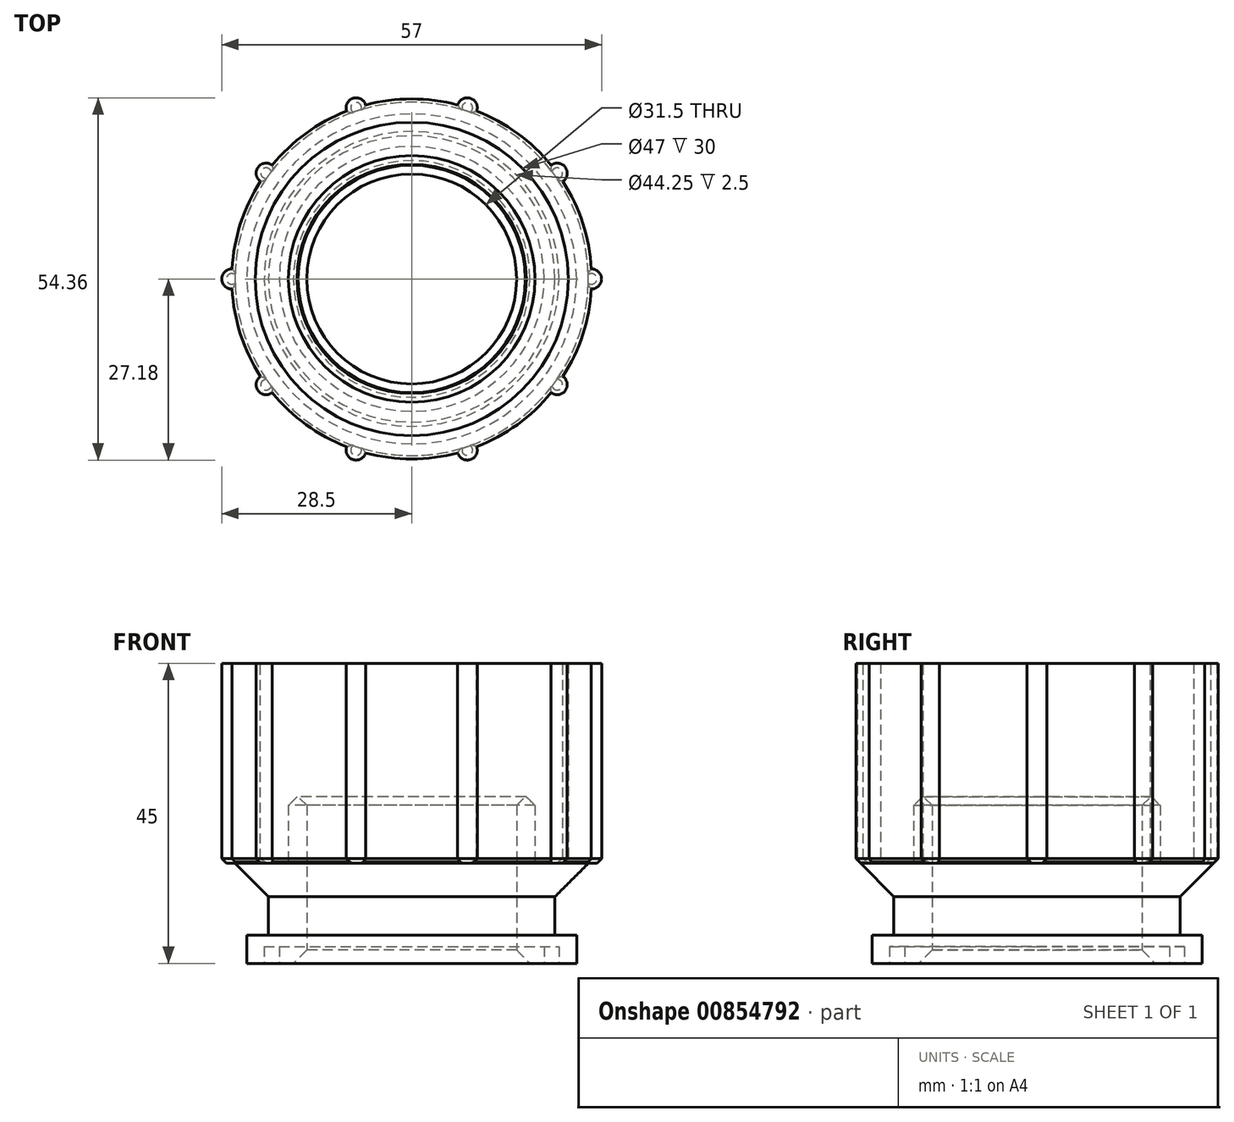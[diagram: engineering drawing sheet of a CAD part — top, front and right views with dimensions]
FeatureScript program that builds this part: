
annotation { "Feature Type Name" : "Feature", "Feature Type Description" : "" }
export const myFeature = defineFeature(function(context is Context, id is Id, definition is map)
    precondition{}
    {
        {
            var Q0;
            Q0=qCreatedBy(makeId("Top.planeOp"),FACE);
            var sketch = newSketch(context, id + "F0", { "sketchPlane" : qUnion([Q0])});
            skCircle(sketch, "E0", {"center": v(0, 0) * mm, "radius": 24.75 * mm});
            skCircle(sketch, "E1", {"center": v(0, 0) * mm, "radius": 15.75 * mm});
            skSolve(sketch);
        }
        {
            var Q0;
            Q0=makeQuery(id+"F0.imprint","IMPRINT",FACE,{"disambiguationData":[TD([[makeQuery(id+"F0.imprint","IMPRINT",EDGE,{"derivedFrom":sQuery(id+"F0.wireOp",EDGE,"E0")}),1.0]])]});
            extrude(context, id + "F1", {"entities" : qUnion([Q0]), "depth" : 4.25 * mm, "offsetDistance" : 25 * mm});
        }
        {
            var Q0;
            Q0=makeQuery(id+"F1.opExtrude","CAP_FACE",FACE,{"disambiguationData":[OSD([sQuery(id+"F0.wireOp",EDGE,"E0"),sQuery(id+"F0.wireOp",EDGE,"E1")])],"isStart":false});
            var sketch = newSketch(context, id + "F2", { "sketchPlane" : qUnion([Q0])});
            skCircle(sketch, "E2", {"center": v(0, 0) * mm, "radius": 21.5 * mm});
            skSolve(sketch);
        }
        {
            var Q0;
            Q0=makeQuery(id+"F2.imprint","IMPRINT",FACE,{"disambiguationData":[TD([[makeQuery(id+"F2.imprint","IMPRINT",EDGE,{"derivedFrom":sQuery(id+"F2.wireOp",EDGE,"E2")}),1.0]])]});
            extrude(context, id + "F3", {"entities" : qUnion([Q0]), "operationType" : NewBodyOperationType.ADD, "depth" : 4 * mm, "offsetDistance" : 25 * mm});
        }
        {
            var Q0;
            Q0=makeQuery(id+"F3.opExtrude","CAP_FACE",FACE,{"disambiguationData":[OSD([sQuery(id+"F0.wireOp",EDGE,"E1"),sQuery(id+"F2.wireOp",EDGE,"E2")])],"isStart":false});
            var sketch = newSketch(context, id + "F4", { "sketchPlane" : qUnion([Q0])});
            skCircle(sketch, "E3", {"center": v(0, 0) * mm, "radius": 26.5 * mm});
            skSolve(sketch);
        }
        {
            var Q0;
            Q0=makeQuery(id+"F4.imprint","IMPRINT",FACE,{"disambiguationData":[TD([[makeQuery(id+"F4.imprint","IMPRINT",EDGE,{"derivedFrom":sQuery(id+"F4.wireOp",EDGE,"E3")}),1.0]])]});
            var Q1;
            Q1=makeQuery(id+"F4.imprint","IMPRINT",FACE,{"disambiguationData":[TD([[makeQuery(id+"F4.imprint","IMPRINT",EDGE,{"derivedFrom":makeQuery(id+"F3.opExtrude","CAP_EDGE",EDGE,{"disambiguationData":[OSD([sQuery(id+"F2.wireOp",EDGE,"E2")])],"isStart":false})}),1.0]])]});
            extrude(context, id + "F5", {"entities" : qUnion([Q0, Q1]), "operationType" : NewBodyOperationType.ADD, "depth" : 6.75 * mm, "offsetDistance" : 25 * mm});
        }
        {
            var Q0;
            Q0=makeQuery(id+"F5.opExtrude","CAP_FACE",FACE,{"disambiguationData":[OSD([sQuery(id+"F0.wireOp",EDGE,"E1"),sQuery(id+"F4.wireOp",EDGE,"E3")])],"isStart":false});
            var sketch = newSketch(context, id + "F6", { "sketchPlane" : qUnion([Q0])});
            skCircle(sketch, "E4", {"center": v(0, 0) * mm, "radius": 27 * mm});
            skCircle(sketch, "E5", {"center": v(0, 0) * mm, "radius": 23.5 * mm});
            skSolve(sketch);
        }
        {
            var Q0;
            Q0=makeQuery(id+"F6.imprint","IMPRINT",FACE,{"disambiguationData":[TD([[makeQuery(id+"F6.imprint","IMPRINT",EDGE,{"derivedFrom":makeQuery(id+"F5.opExtrude","CAP_EDGE",EDGE,{"disambiguationData":[OSD([sQuery(id+"F4.wireOp",EDGE,"E3")])],"isStart":false})}),1.0]])]});
            var Q1;
            Q1=makeQuery(id+"F6.imprint","IMPRINT",FACE,{"disambiguationData":[TD([[makeQuery(id+"F6.imprint","IMPRINT",EDGE,{"derivedFrom":sQuery(id+"F6.wireOp",EDGE,"E4")}),1.0]])]});
            extrude(context, id + "F7", {"entities" : qUnion([Q0, Q1]), "operationType" : NewBodyOperationType.ADD, "depth" : 30 * mm, "offsetDistance" : 25 * mm});
        }
        {
            var Q0;
            Q0=makeQuery(id+"F5.opExtrude","CAP_FACE",FACE,{"disambiguationData":[OSD([sQuery(id+"F0.wireOp",EDGE,"E1"),sQuery(id+"F4.wireOp",EDGE,"E3")])],"isStart":false});
            var sketch = newSketch(context, id + "F8", { "sketchPlane" : qUnion([Q0])});
            skCircle(sketch, "E6", {"center": v(0, 0) * mm, "radius": 18.5 * mm});
            skSolve(sketch);
        }
        {
            var Q0;
            Q0=makeQuery(id+"F8.imprint","IMPRINT",FACE,{"disambiguationData":[TD([[makeQuery(id+"F8.imprint","IMPRINT",EDGE,{"derivedFrom":sQuery(id+"F8.wireOp",EDGE,"E6")}),1.0]])]});
            extrude(context, id + "F9", {"entities" : qUnion([Q0]), "operationType" : NewBodyOperationType.ADD, "depth" : 10 * mm, "offsetDistance" : 25 * mm});
        }
        {
            var Q0;
            Q0=makeQuery(id+"F1.opExtrude","CAP_FACE",FACE,{"disambiguationData":[OSD([sQuery(id+"F0.wireOp",EDGE,"E0"),sQuery(id+"F0.wireOp",EDGE,"E1")])],"isStart":true});
            var sketch = newSketch(context, id + "F10", { "sketchPlane" : qUnion([Q0])});
            skCircle(sketch, "E7", {"center": v(0, 0) * mm, "radius": 22.12 * mm});
            skCircle(sketch, "E8", {"center": v(0, 0) * mm, "radius": 19.88 * mm});
            skSolve(sketch);
        }
        {
            var Q0;
            Q0=makeQuery(id+"F10.imprint","IMPRINT",FACE,{"disambiguationData":[TD([[makeQuery(id+"F10.imprint","IMPRINT",EDGE,{"derivedFrom":sQuery(id+"F10.wireOp",EDGE,"E7")}),1.0]])]});
            extrude(context, id + "F11", {"entities" : qUnion([Q0]), "operationType" : NewBodyOperationType.REMOVE, "oppositeDirection" : true, "depth" : 2.5 * mm, "offsetDistance" : 25 * mm});
        }
        {
            var Q0;
            Q0=makeQuery(id+"F7.opExtrude","CAP_FACE",FACE,{"disambiguationData":[OSD([sQuery(id+"F6.wireOp",EDGE,"E4"),sQuery(id+"F6.wireOp",EDGE,"E5")])],"isStart":false});
            var sketch = newSketch(context, id + "F12", { "sketchPlane" : qUnion([Q0])});
            skArc(sketch, "E9", {"start": v(26.96, -1.5) * mm, "mid": v(28.5, 0) * mm, "end": v(26.96, 1.5) * mm});
            skArc(sketch, "E10.1.0", {"start": v(22.7, 14.63) * mm, "mid": v(23.06, 16.75) * mm, "end": v(20.93, 17.06) * mm});
            skArc(sketch, "E10.2.0", {"start": v(9.76, 25.18) * mm, "mid": v(8.8, 27.1) * mm, "end": v(6.9, 26.1) * mm});
            skArc(sketch, "E10.3.0", {"start": v(-6.9, 26.1) * mm, "mid": v(-8.8, 27.1) * mm, "end": v(-9.76, 25.18) * mm});
            skArc(sketch, "E10.4.0", {"start": v(-20.93, 17.06) * mm, "mid": v(-23.06, 16.75) * mm, "end": v(-22.7, 14.63) * mm});
            skArc(sketch, "E10.5.0", {"start": v(-26.96, 1.5) * mm, "mid": v(-28.5, 0) * mm, "end": v(-26.96, -1.5) * mm});
            skArc(sketch, "E10.6.0", {"start": v(-22.7, -14.63) * mm, "mid": v(-23.06, -16.75) * mm, "end": v(-20.93, -17.06) * mm});
            skArc(sketch, "E10.7.0", {"start": v(-9.76, -25.18) * mm, "mid": v(-8.8, -27.1) * mm, "end": v(-6.9, -26.1) * mm});
            skArc(sketch, "E10.8.0", {"start": v(6.9, -26.1) * mm, "mid": v(8.8, -27.1) * mm, "end": v(9.76, -25.18) * mm});
            skArc(sketch, "E10.9.0", {"start": v(20.93, -17.06) * mm, "mid": v(23.06, -16.75) * mm, "end": v(22.7, -14.63) * mm});
            skPoint(sketch, "E10.center", {"position": v(0, 0) * mm});
            skSolve(sketch);
        }
        {
            var Q0;
            {var subQ0=sQuery(id+"F12.wireOp",EDGE,"E10.1.0");Q0=makeQuery(id+"F12.imprint","IMPRINT",FACE,{"disambiguationData":[TD([[makeQuery(id+"F12.imprint","IMPRINT",EDGE,{"derivedFrom":subQ0}),1.0]])]});}
            var Q1;
            {var subQ0=sQuery(id+"F12.wireOp",EDGE,"E10.2.0");Q1=makeQuery(id+"F12.imprint","IMPRINT",FACE,{"disambiguationData":[TD([[makeQuery(id+"F12.imprint","IMPRINT",EDGE,{"derivedFrom":subQ0}),1.0]])]});}
            var Q2;
            {var subQ0=sQuery(id+"F12.wireOp",EDGE,"E10.3.0");Q2=makeQuery(id+"F12.imprint","IMPRINT",FACE,{"disambiguationData":[TD([[makeQuery(id+"F12.imprint","IMPRINT",EDGE,{"derivedFrom":subQ0}),1.0]])]});}
            var Q3;
            {var subQ0=sQuery(id+"F12.wireOp",EDGE,"E10.4.0");Q3=makeQuery(id+"F12.imprint","IMPRINT",FACE,{"disambiguationData":[TD([[makeQuery(id+"F12.imprint","IMPRINT",EDGE,{"derivedFrom":subQ0}),1.0]])]});}
            var Q4;
            {var subQ0=sQuery(id+"F12.wireOp",EDGE,"E10.5.0");Q4=makeQuery(id+"F12.imprint","IMPRINT",FACE,{"disambiguationData":[TD([[makeQuery(id+"F12.imprint","IMPRINT",EDGE,{"derivedFrom":subQ0}),1.0]])]});}
            var Q5;
            {var subQ0=sQuery(id+"F12.wireOp",EDGE,"E10.6.0");Q5=makeQuery(id+"F12.imprint","IMPRINT",FACE,{"disambiguationData":[TD([[makeQuery(id+"F12.imprint","IMPRINT",EDGE,{"derivedFrom":subQ0}),1.0]])]});}
            var Q6;
            {var subQ0=sQuery(id+"F12.wireOp",EDGE,"E10.7.0");Q6=makeQuery(id+"F12.imprint","IMPRINT",FACE,{"disambiguationData":[TD([[makeQuery(id+"F12.imprint","IMPRINT",EDGE,{"derivedFrom":subQ0}),1.0]])]});}
            var Q7;
            {var subQ0=sQuery(id+"F12.wireOp",EDGE,"E10.8.0");Q7=makeQuery(id+"F12.imprint","IMPRINT",FACE,{"disambiguationData":[TD([[makeQuery(id+"F12.imprint","IMPRINT",EDGE,{"derivedFrom":subQ0}),1.0]])]});}
            var Q8;
            {var subQ0=sQuery(id+"F12.wireOp",EDGE,"E10.9.0");Q8=makeQuery(id+"F12.imprint","IMPRINT",FACE,{"disambiguationData":[TD([[makeQuery(id+"F12.imprint","IMPRINT",EDGE,{"derivedFrom":subQ0}),1.0]])]});}
            var Q9;
            {var subQ0=sQuery(id+"F12.wireOp",EDGE,"E9");Q9=makeQuery(id+"F12.imprint","IMPRINT",FACE,{"disambiguationData":[TD([[makeQuery(id+"F12.imprint","IMPRINT",EDGE,{"derivedFrom":subQ0}),1.0]])]});}
            var Q10;
            Q10=makeQuery(id+"F7.opExtrude","CAP_FACE",FACE,{"disambiguationData":[OSD([sQuery(id+"F6.wireOp",EDGE,"E4"),sQuery(id+"F6.wireOp",EDGE,"E5")])],"isStart":true});
            extrude(context, id + "F13", {"entities" : qUnion([Q0, Q1, Q2, Q3, Q4, Q5, Q6, Q7, Q8, Q9]), "operationType" : NewBodyOperationType.ADD, "endBound" : BoundingType.UP_TO_SURFACE, "oppositeDirection" : true, "depth" : 25 * mm, "endBoundEntityFace" : qUnion([Q10]), "offsetDistance" : 25 * mm});
        }
        {
            var Q0;
            Q0=makeQuery(id+"F1.opExtrude","CAP_EDGE",EDGE,{"disambiguationData":[OSD([sQuery(id+"F0.wireOp",EDGE,"E1")])],"isStart":true});
            chamfer(context, id + "F14", {"entities" : qUnion([Q0]), "width" : 2 * mm, "tangentPropagation" : true});
        }
        {
            var Q0;
            {var subQ0=sQuery(id+"F12.wireOp",EDGE,"E10.5.0");var subQ1=sQuery(id+"F6.wireOp",EDGE,"E4");var subQ2=sQuery(id+"F12.wireOp",EDGE,"E10.6.0");Q0=makeQuery(id+"F13.boolean.opBoolean","SPLIT",EDGE,{"disambiguationData":[TD([makeQuery(id+"F7.opExtrude","SWEPT_FACE",FACE,{"disambiguationData":[OSD([subQ1])]}),makeQuery(id+"F7.opExtrude","CAP_FACE",FACE,{"disambiguationData":[OSD([subQ1,sQuery(id+"F6.wireOp",EDGE,"E5")])],"isStart":true}),makeQuery(id+"F13.opExtrude","CAP_FACE",FACE,{"disambiguationData":[OSD([subQ1,sQuery(id+"F12.wireOp",EDGE,"E9")])],"isStart":false}),makeQuery(id+"F13.opExtrude","CAP_FACE",FACE,{"disambiguationData":[OSD([subQ1,sQuery(id+"F12.wireOp",EDGE,"E10.1.0")])],"isStart":false}),makeQuery(id+"F13.opExtrude","CAP_FACE",FACE,{"disambiguationData":[OSD([subQ1,sQuery(id+"F12.wireOp",EDGE,"E10.2.0")])],"isStart":false}),makeQuery(id+"F13.opExtrude","CAP_FACE",FACE,{"disambiguationData":[OSD([subQ1,sQuery(id+"F12.wireOp",EDGE,"E10.3.0")])],"isStart":false}),makeQuery(id+"F13.opExtrude","CAP_FACE",FACE,{"disambiguationData":[OSD([subQ1,sQuery(id+"F12.wireOp",EDGE,"E10.4.0")])],"isStart":false}),makeQuery(id+"F13.opExtrude","SWEPT_FACE",FACE,{"disambiguationData":[OSD([subQ0])]}),makeQuery(id+"F13.opExtrude","CAP_FACE",FACE,{"disambiguationData":[OSD([subQ1,subQ0])],"isStart":false}),makeQuery(id+"F13.opExtrude","SWEPT_FACE",FACE,{"disambiguationData":[OSD([subQ2])]}),makeQuery(id+"F13.opExtrude","CAP_FACE",FACE,{"disambiguationData":[OSD([subQ1,subQ2])],"isStart":false}),makeQuery(id+"F13.opExtrude","CAP_FACE",FACE,{"disambiguationData":[OSD([subQ1,sQuery(id+"F12.wireOp",EDGE,"E10.7.0")])],"isStart":false}),makeQuery(id+"F13.opExtrude","CAP_FACE",FACE,{"disambiguationData":[OSD([subQ1,sQuery(id+"F12.wireOp",EDGE,"E10.8.0")])],"isStart":false}),makeQuery(id+"F13.opExtrude","CAP_FACE",FACE,{"disambiguationData":[OSD([subQ1,sQuery(id+"F12.wireOp",EDGE,"E10.9.0")])],"isStart":false})])],"derivedFrom":makeQuery(id+"F7.opExtrude","CAP_EDGE",EDGE,{"disambiguationData":[OSD([subQ1])],"isStart":true})});}
            var Q1;
            Q1=makeQuery(id+"F13.opExtrude","CAP_EDGE",EDGE,{"disambiguationData":[OSD([sQuery(id+"F12.wireOp",EDGE,"E10.5.0")])],"isStart":false});
            var Q2;
            {var subQ0=sQuery(id+"F12.wireOp",EDGE,"E10.5.0");var subQ1=sQuery(id+"F6.wireOp",EDGE,"E4");var subQ2=sQuery(id+"F12.wireOp",EDGE,"E10.4.0");Q2=makeQuery(id+"F13.boolean.opBoolean","SPLIT",EDGE,{"disambiguationData":[TD([makeQuery(id+"F7.opExtrude","SWEPT_FACE",FACE,{"disambiguationData":[OSD([subQ1])]}),makeQuery(id+"F7.opExtrude","CAP_FACE",FACE,{"disambiguationData":[OSD([subQ1,sQuery(id+"F6.wireOp",EDGE,"E5")])],"isStart":true}),makeQuery(id+"F13.opExtrude","CAP_FACE",FACE,{"disambiguationData":[OSD([subQ1,sQuery(id+"F12.wireOp",EDGE,"E9")])],"isStart":false}),makeQuery(id+"F13.opExtrude","CAP_FACE",FACE,{"disambiguationData":[OSD([subQ1,sQuery(id+"F12.wireOp",EDGE,"E10.1.0")])],"isStart":false}),makeQuery(id+"F13.opExtrude","CAP_FACE",FACE,{"disambiguationData":[OSD([subQ1,sQuery(id+"F12.wireOp",EDGE,"E10.2.0")])],"isStart":false}),makeQuery(id+"F13.opExtrude","CAP_FACE",FACE,{"disambiguationData":[OSD([subQ1,sQuery(id+"F12.wireOp",EDGE,"E10.3.0")])],"isStart":false}),makeQuery(id+"F13.opExtrude","SWEPT_FACE",FACE,{"disambiguationData":[OSD([subQ2])]}),makeQuery(id+"F13.opExtrude","CAP_FACE",FACE,{"disambiguationData":[OSD([subQ1,subQ2])],"isStart":false}),makeQuery(id+"F13.opExtrude","SWEPT_FACE",FACE,{"disambiguationData":[OSD([subQ0])]}),makeQuery(id+"F13.opExtrude","CAP_FACE",FACE,{"disambiguationData":[OSD([subQ1,subQ0])],"isStart":false}),makeQuery(id+"F13.opExtrude","CAP_FACE",FACE,{"disambiguationData":[OSD([subQ1,sQuery(id+"F12.wireOp",EDGE,"E10.6.0")])],"isStart":false}),makeQuery(id+"F13.opExtrude","CAP_FACE",FACE,{"disambiguationData":[OSD([subQ1,sQuery(id+"F12.wireOp",EDGE,"E10.7.0")])],"isStart":false}),makeQuery(id+"F13.opExtrude","CAP_FACE",FACE,{"disambiguationData":[OSD([subQ1,sQuery(id+"F12.wireOp",EDGE,"E10.8.0")])],"isStart":false}),makeQuery(id+"F13.opExtrude","CAP_FACE",FACE,{"disambiguationData":[OSD([subQ1,sQuery(id+"F12.wireOp",EDGE,"E10.9.0")])],"isStart":false})])],"derivedFrom":makeQuery(id+"F7.opExtrude","CAP_EDGE",EDGE,{"disambiguationData":[OSD([subQ1])],"isStart":true})});}
            var Q3;
            Q3=makeQuery(id+"F13.opExtrude","CAP_EDGE",EDGE,{"disambiguationData":[OSD([sQuery(id+"F12.wireOp",EDGE,"E10.4.0")])],"isStart":false});
            var Q4;
            {var subQ0=sQuery(id+"F6.wireOp",EDGE,"E4");var subQ1=sQuery(id+"F12.wireOp",EDGE,"E10.4.0");var subQ2=sQuery(id+"F12.wireOp",EDGE,"E10.3.0");Q4=makeQuery(id+"F13.boolean.opBoolean","SPLIT",EDGE,{"disambiguationData":[TD([makeQuery(id+"F7.opExtrude","SWEPT_FACE",FACE,{"disambiguationData":[OSD([subQ0])]}),makeQuery(id+"F7.opExtrude","CAP_FACE",FACE,{"disambiguationData":[OSD([subQ0,sQuery(id+"F6.wireOp",EDGE,"E5")])],"isStart":true}),makeQuery(id+"F13.opExtrude","CAP_FACE",FACE,{"disambiguationData":[OSD([subQ0,sQuery(id+"F12.wireOp",EDGE,"E9")])],"isStart":false}),makeQuery(id+"F13.opExtrude","CAP_FACE",FACE,{"disambiguationData":[OSD([subQ0,sQuery(id+"F12.wireOp",EDGE,"E10.1.0")])],"isStart":false}),makeQuery(id+"F13.opExtrude","CAP_FACE",FACE,{"disambiguationData":[OSD([subQ0,sQuery(id+"F12.wireOp",EDGE,"E10.2.0")])],"isStart":false}),makeQuery(id+"F13.opExtrude","SWEPT_FACE",FACE,{"disambiguationData":[OSD([subQ2])]}),makeQuery(id+"F13.opExtrude","CAP_FACE",FACE,{"disambiguationData":[OSD([subQ0,subQ2])],"isStart":false}),makeQuery(id+"F13.opExtrude","SWEPT_FACE",FACE,{"disambiguationData":[OSD([subQ1])]}),makeQuery(id+"F13.opExtrude","CAP_FACE",FACE,{"disambiguationData":[OSD([subQ0,subQ1])],"isStart":false}),makeQuery(id+"F13.opExtrude","CAP_FACE",FACE,{"disambiguationData":[OSD([subQ0,sQuery(id+"F12.wireOp",EDGE,"E10.5.0")])],"isStart":false}),makeQuery(id+"F13.opExtrude","CAP_FACE",FACE,{"disambiguationData":[OSD([subQ0,sQuery(id+"F12.wireOp",EDGE,"E10.6.0")])],"isStart":false}),makeQuery(id+"F13.opExtrude","CAP_FACE",FACE,{"disambiguationData":[OSD([subQ0,sQuery(id+"F12.wireOp",EDGE,"E10.7.0")])],"isStart":false}),makeQuery(id+"F13.opExtrude","CAP_FACE",FACE,{"disambiguationData":[OSD([subQ0,sQuery(id+"F12.wireOp",EDGE,"E10.8.0")])],"isStart":false}),makeQuery(id+"F13.opExtrude","CAP_FACE",FACE,{"disambiguationData":[OSD([subQ0,sQuery(id+"F12.wireOp",EDGE,"E10.9.0")])],"isStart":false})])],"derivedFrom":makeQuery(id+"F7.opExtrude","CAP_EDGE",EDGE,{"disambiguationData":[OSD([subQ0])],"isStart":true})});}
            var Q5;
            Q5=makeQuery(id+"F13.opExtrude","CAP_EDGE",EDGE,{"disambiguationData":[OSD([sQuery(id+"F12.wireOp",EDGE,"E10.3.0")])],"isStart":false});
            var Q6;
            {var subQ0=sQuery(id+"F6.wireOp",EDGE,"E4");var subQ1=sQuery(id+"F12.wireOp",EDGE,"E10.3.0");var subQ2=sQuery(id+"F12.wireOp",EDGE,"E10.2.0");Q6=makeQuery(id+"F13.boolean.opBoolean","SPLIT",EDGE,{"disambiguationData":[TD([makeQuery(id+"F7.opExtrude","SWEPT_FACE",FACE,{"disambiguationData":[OSD([subQ0])]}),makeQuery(id+"F7.opExtrude","CAP_FACE",FACE,{"disambiguationData":[OSD([subQ0,sQuery(id+"F6.wireOp",EDGE,"E5")])],"isStart":true}),makeQuery(id+"F13.opExtrude","CAP_FACE",FACE,{"disambiguationData":[OSD([subQ0,sQuery(id+"F12.wireOp",EDGE,"E9")])],"isStart":false}),makeQuery(id+"F13.opExtrude","CAP_FACE",FACE,{"disambiguationData":[OSD([subQ0,sQuery(id+"F12.wireOp",EDGE,"E10.1.0")])],"isStart":false}),makeQuery(id+"F13.opExtrude","SWEPT_FACE",FACE,{"disambiguationData":[OSD([subQ2])]}),makeQuery(id+"F13.opExtrude","CAP_FACE",FACE,{"disambiguationData":[OSD([subQ0,subQ2])],"isStart":false}),makeQuery(id+"F13.opExtrude","SWEPT_FACE",FACE,{"disambiguationData":[OSD([subQ1])]}),makeQuery(id+"F13.opExtrude","CAP_FACE",FACE,{"disambiguationData":[OSD([subQ0,subQ1])],"isStart":false}),makeQuery(id+"F13.opExtrude","CAP_FACE",FACE,{"disambiguationData":[OSD([subQ0,sQuery(id+"F12.wireOp",EDGE,"E10.4.0")])],"isStart":false}),makeQuery(id+"F13.opExtrude","CAP_FACE",FACE,{"disambiguationData":[OSD([subQ0,sQuery(id+"F12.wireOp",EDGE,"E10.5.0")])],"isStart":false}),makeQuery(id+"F13.opExtrude","CAP_FACE",FACE,{"disambiguationData":[OSD([subQ0,sQuery(id+"F12.wireOp",EDGE,"E10.6.0")])],"isStart":false}),makeQuery(id+"F13.opExtrude","CAP_FACE",FACE,{"disambiguationData":[OSD([subQ0,sQuery(id+"F12.wireOp",EDGE,"E10.7.0")])],"isStart":false}),makeQuery(id+"F13.opExtrude","CAP_FACE",FACE,{"disambiguationData":[OSD([subQ0,sQuery(id+"F12.wireOp",EDGE,"E10.8.0")])],"isStart":false}),makeQuery(id+"F13.opExtrude","CAP_FACE",FACE,{"disambiguationData":[OSD([subQ0,sQuery(id+"F12.wireOp",EDGE,"E10.9.0")])],"isStart":false})])],"derivedFrom":makeQuery(id+"F7.opExtrude","CAP_EDGE",EDGE,{"disambiguationData":[OSD([subQ0])],"isStart":true})});}
            var Q7;
            Q7=makeQuery(id+"F13.opExtrude","CAP_EDGE",EDGE,{"disambiguationData":[OSD([sQuery(id+"F12.wireOp",EDGE,"E10.2.0")])],"isStart":false});
            var Q8;
            {var subQ0=sQuery(id+"F6.wireOp",EDGE,"E4");var subQ1=sQuery(id+"F12.wireOp",EDGE,"E10.2.0");var subQ2=sQuery(id+"F12.wireOp",EDGE,"E10.1.0");Q8=makeQuery(id+"F13.boolean.opBoolean","SPLIT",EDGE,{"disambiguationData":[TD([makeQuery(id+"F7.opExtrude","SWEPT_FACE",FACE,{"disambiguationData":[OSD([subQ0])]}),makeQuery(id+"F7.opExtrude","CAP_FACE",FACE,{"disambiguationData":[OSD([subQ0,sQuery(id+"F6.wireOp",EDGE,"E5")])],"isStart":true}),makeQuery(id+"F13.opExtrude","CAP_FACE",FACE,{"disambiguationData":[OSD([subQ0,sQuery(id+"F12.wireOp",EDGE,"E9")])],"isStart":false}),makeQuery(id+"F13.opExtrude","SWEPT_FACE",FACE,{"disambiguationData":[OSD([subQ2])]}),makeQuery(id+"F13.opExtrude","CAP_FACE",FACE,{"disambiguationData":[OSD([subQ0,subQ2])],"isStart":false}),makeQuery(id+"F13.opExtrude","SWEPT_FACE",FACE,{"disambiguationData":[OSD([subQ1])]}),makeQuery(id+"F13.opExtrude","CAP_FACE",FACE,{"disambiguationData":[OSD([subQ0,subQ1])],"isStart":false}),makeQuery(id+"F13.opExtrude","CAP_FACE",FACE,{"disambiguationData":[OSD([subQ0,sQuery(id+"F12.wireOp",EDGE,"E10.3.0")])],"isStart":false}),makeQuery(id+"F13.opExtrude","CAP_FACE",FACE,{"disambiguationData":[OSD([subQ0,sQuery(id+"F12.wireOp",EDGE,"E10.4.0")])],"isStart":false}),makeQuery(id+"F13.opExtrude","CAP_FACE",FACE,{"disambiguationData":[OSD([subQ0,sQuery(id+"F12.wireOp",EDGE,"E10.5.0")])],"isStart":false}),makeQuery(id+"F13.opExtrude","CAP_FACE",FACE,{"disambiguationData":[OSD([subQ0,sQuery(id+"F12.wireOp",EDGE,"E10.6.0")])],"isStart":false}),makeQuery(id+"F13.opExtrude","CAP_FACE",FACE,{"disambiguationData":[OSD([subQ0,sQuery(id+"F12.wireOp",EDGE,"E10.7.0")])],"isStart":false}),makeQuery(id+"F13.opExtrude","CAP_FACE",FACE,{"disambiguationData":[OSD([subQ0,sQuery(id+"F12.wireOp",EDGE,"E10.8.0")])],"isStart":false}),makeQuery(id+"F13.opExtrude","CAP_FACE",FACE,{"disambiguationData":[OSD([subQ0,sQuery(id+"F12.wireOp",EDGE,"E10.9.0")])],"isStart":false})])],"derivedFrom":makeQuery(id+"F7.opExtrude","CAP_EDGE",EDGE,{"disambiguationData":[OSD([subQ0])],"isStart":true})});}
            var Q9;
            Q9=makeQuery(id+"F13.opExtrude","CAP_EDGE",EDGE,{"disambiguationData":[OSD([sQuery(id+"F12.wireOp",EDGE,"E10.1.0")])],"isStart":false});
            var Q10;
            {var subQ0=sQuery(id+"F6.wireOp",EDGE,"E4");var subQ1=sQuery(id+"F12.wireOp",EDGE,"E10.1.0");var subQ2=sQuery(id+"F12.wireOp",EDGE,"E9");Q10=makeQuery(id+"F13.boolean.opBoolean","SPLIT",EDGE,{"disambiguationData":[TD([makeQuery(id+"F7.opExtrude","SWEPT_FACE",FACE,{"disambiguationData":[OSD([subQ0])]}),makeQuery(id+"F7.opExtrude","CAP_FACE",FACE,{"disambiguationData":[OSD([subQ0,sQuery(id+"F6.wireOp",EDGE,"E5")])],"isStart":true}),makeQuery(id+"F13.opExtrude","SWEPT_FACE",FACE,{"disambiguationData":[OSD([subQ2])]}),makeQuery(id+"F13.opExtrude","CAP_FACE",FACE,{"disambiguationData":[OSD([subQ0,subQ2])],"isStart":false}),makeQuery(id+"F13.opExtrude","SWEPT_FACE",FACE,{"disambiguationData":[OSD([subQ1])]}),makeQuery(id+"F13.opExtrude","CAP_FACE",FACE,{"disambiguationData":[OSD([subQ0,subQ1])],"isStart":false}),makeQuery(id+"F13.opExtrude","CAP_FACE",FACE,{"disambiguationData":[OSD([subQ0,sQuery(id+"F12.wireOp",EDGE,"E10.2.0")])],"isStart":false}),makeQuery(id+"F13.opExtrude","CAP_FACE",FACE,{"disambiguationData":[OSD([subQ0,sQuery(id+"F12.wireOp",EDGE,"E10.3.0")])],"isStart":false}),makeQuery(id+"F13.opExtrude","CAP_FACE",FACE,{"disambiguationData":[OSD([subQ0,sQuery(id+"F12.wireOp",EDGE,"E10.4.0")])],"isStart":false}),makeQuery(id+"F13.opExtrude","CAP_FACE",FACE,{"disambiguationData":[OSD([subQ0,sQuery(id+"F12.wireOp",EDGE,"E10.5.0")])],"isStart":false}),makeQuery(id+"F13.opExtrude","CAP_FACE",FACE,{"disambiguationData":[OSD([subQ0,sQuery(id+"F12.wireOp",EDGE,"E10.6.0")])],"isStart":false}),makeQuery(id+"F13.opExtrude","CAP_FACE",FACE,{"disambiguationData":[OSD([subQ0,sQuery(id+"F12.wireOp",EDGE,"E10.7.0")])],"isStart":false}),makeQuery(id+"F13.opExtrude","CAP_FACE",FACE,{"disambiguationData":[OSD([subQ0,sQuery(id+"F12.wireOp",EDGE,"E10.8.0")])],"isStart":false}),makeQuery(id+"F13.opExtrude","CAP_FACE",FACE,{"disambiguationData":[OSD([subQ0,sQuery(id+"F12.wireOp",EDGE,"E10.9.0")])],"isStart":false})])],"derivedFrom":makeQuery(id+"F7.opExtrude","CAP_EDGE",EDGE,{"disambiguationData":[OSD([subQ0])],"isStart":true})});}
            var Q11;
            {var subQ0=sQuery(id+"F6.wireOp",EDGE,"E4");var subQ1=sQuery(id+"F12.wireOp",EDGE,"E9");var subQ2=sQuery(id+"F12.wireOp",EDGE,"E10.9.0");Q11=makeQuery(id+"F13.boolean.opBoolean","SPLIT",EDGE,{"disambiguationData":[TD([makeQuery(id+"F7.opExtrude","SWEPT_FACE",FACE,{"disambiguationData":[OSD([subQ0])]}),makeQuery(id+"F7.opExtrude","CAP_FACE",FACE,{"disambiguationData":[OSD([subQ0,sQuery(id+"F6.wireOp",EDGE,"E5")])],"isStart":true}),makeQuery(id+"F13.opExtrude","SWEPT_FACE",FACE,{"disambiguationData":[OSD([subQ1])]}),makeQuery(id+"F13.opExtrude","CAP_FACE",FACE,{"disambiguationData":[OSD([subQ0,subQ1])],"isStart":false}),makeQuery(id+"F13.opExtrude","CAP_FACE",FACE,{"disambiguationData":[OSD([subQ0,sQuery(id+"F12.wireOp",EDGE,"E10.1.0")])],"isStart":false}),makeQuery(id+"F13.opExtrude","CAP_FACE",FACE,{"disambiguationData":[OSD([subQ0,sQuery(id+"F12.wireOp",EDGE,"E10.2.0")])],"isStart":false}),makeQuery(id+"F13.opExtrude","CAP_FACE",FACE,{"disambiguationData":[OSD([subQ0,sQuery(id+"F12.wireOp",EDGE,"E10.3.0")])],"isStart":false}),makeQuery(id+"F13.opExtrude","CAP_FACE",FACE,{"disambiguationData":[OSD([subQ0,sQuery(id+"F12.wireOp",EDGE,"E10.4.0")])],"isStart":false}),makeQuery(id+"F13.opExtrude","CAP_FACE",FACE,{"disambiguationData":[OSD([subQ0,sQuery(id+"F12.wireOp",EDGE,"E10.5.0")])],"isStart":false}),makeQuery(id+"F13.opExtrude","CAP_FACE",FACE,{"disambiguationData":[OSD([subQ0,sQuery(id+"F12.wireOp",EDGE,"E10.6.0")])],"isStart":false}),makeQuery(id+"F13.opExtrude","CAP_FACE",FACE,{"disambiguationData":[OSD([subQ0,sQuery(id+"F12.wireOp",EDGE,"E10.7.0")])],"isStart":false}),makeQuery(id+"F13.opExtrude","CAP_FACE",FACE,{"disambiguationData":[OSD([subQ0,sQuery(id+"F12.wireOp",EDGE,"E10.8.0")])],"isStart":false}),makeQuery(id+"F13.opExtrude","SWEPT_FACE",FACE,{"disambiguationData":[OSD([subQ2])]}),makeQuery(id+"F13.opExtrude","CAP_FACE",FACE,{"disambiguationData":[OSD([subQ0,subQ2])],"isStart":false})])],"derivedFrom":makeQuery(id+"F7.opExtrude","CAP_EDGE",EDGE,{"disambiguationData":[OSD([subQ0])],"isStart":true})});}
            var Q12;
            Q12=makeQuery(id+"F13.opExtrude","CAP_EDGE",EDGE,{"disambiguationData":[OSD([sQuery(id+"F12.wireOp",EDGE,"E9")])],"isStart":false});
            var Q13;
            {var subQ0=sQuery(id+"F6.wireOp",EDGE,"E4");var subQ1=sQuery(id+"F12.wireOp",EDGE,"E10.8.0");var subQ2=sQuery(id+"F12.wireOp",EDGE,"E10.9.0");Q13=makeQuery(id+"F13.boolean.opBoolean","SPLIT",EDGE,{"disambiguationData":[TD([makeQuery(id+"F7.opExtrude","SWEPT_FACE",FACE,{"disambiguationData":[OSD([subQ0])]}),makeQuery(id+"F7.opExtrude","CAP_FACE",FACE,{"disambiguationData":[OSD([subQ0,sQuery(id+"F6.wireOp",EDGE,"E5")])],"isStart":true}),makeQuery(id+"F13.opExtrude","CAP_FACE",FACE,{"disambiguationData":[OSD([subQ0,sQuery(id+"F12.wireOp",EDGE,"E9")])],"isStart":false}),makeQuery(id+"F13.opExtrude","CAP_FACE",FACE,{"disambiguationData":[OSD([subQ0,sQuery(id+"F12.wireOp",EDGE,"E10.1.0")])],"isStart":false}),makeQuery(id+"F13.opExtrude","CAP_FACE",FACE,{"disambiguationData":[OSD([subQ0,sQuery(id+"F12.wireOp",EDGE,"E10.2.0")])],"isStart":false}),makeQuery(id+"F13.opExtrude","CAP_FACE",FACE,{"disambiguationData":[OSD([subQ0,sQuery(id+"F12.wireOp",EDGE,"E10.3.0")])],"isStart":false}),makeQuery(id+"F13.opExtrude","CAP_FACE",FACE,{"disambiguationData":[OSD([subQ0,sQuery(id+"F12.wireOp",EDGE,"E10.4.0")])],"isStart":false}),makeQuery(id+"F13.opExtrude","CAP_FACE",FACE,{"disambiguationData":[OSD([subQ0,sQuery(id+"F12.wireOp",EDGE,"E10.5.0")])],"isStart":false}),makeQuery(id+"F13.opExtrude","CAP_FACE",FACE,{"disambiguationData":[OSD([subQ0,sQuery(id+"F12.wireOp",EDGE,"E10.6.0")])],"isStart":false}),makeQuery(id+"F13.opExtrude","CAP_FACE",FACE,{"disambiguationData":[OSD([subQ0,sQuery(id+"F12.wireOp",EDGE,"E10.7.0")])],"isStart":false}),makeQuery(id+"F13.opExtrude","SWEPT_FACE",FACE,{"disambiguationData":[OSD([subQ1])]}),makeQuery(id+"F13.opExtrude","CAP_FACE",FACE,{"disambiguationData":[OSD([subQ0,subQ1])],"isStart":false}),makeQuery(id+"F13.opExtrude","SWEPT_FACE",FACE,{"disambiguationData":[OSD([subQ2])]}),makeQuery(id+"F13.opExtrude","CAP_FACE",FACE,{"disambiguationData":[OSD([subQ0,subQ2])],"isStart":false})])],"derivedFrom":makeQuery(id+"F7.opExtrude","CAP_EDGE",EDGE,{"disambiguationData":[OSD([subQ0])],"isStart":true})});}
            var Q14;
            Q14=makeQuery(id+"F13.opExtrude","CAP_EDGE",EDGE,{"disambiguationData":[OSD([sQuery(id+"F12.wireOp",EDGE,"E10.9.0")])],"isStart":false});
            var Q15;
            Q15=makeQuery(id+"F13.opExtrude","CAP_EDGE",EDGE,{"disambiguationData":[OSD([sQuery(id+"F12.wireOp",EDGE,"E10.8.0")])],"isStart":false});
            var Q16;
            {var subQ0=sQuery(id+"F12.wireOp",EDGE,"E10.7.0");var subQ1=sQuery(id+"F6.wireOp",EDGE,"E4");var subQ2=sQuery(id+"F12.wireOp",EDGE,"E10.8.0");Q16=makeQuery(id+"F13.boolean.opBoolean","SPLIT",EDGE,{"disambiguationData":[TD([makeQuery(id+"F7.opExtrude","SWEPT_FACE",FACE,{"disambiguationData":[OSD([subQ1])]}),makeQuery(id+"F7.opExtrude","CAP_FACE",FACE,{"disambiguationData":[OSD([subQ1,sQuery(id+"F6.wireOp",EDGE,"E5")])],"isStart":true}),makeQuery(id+"F13.opExtrude","CAP_FACE",FACE,{"disambiguationData":[OSD([subQ1,sQuery(id+"F12.wireOp",EDGE,"E9")])],"isStart":false}),makeQuery(id+"F13.opExtrude","CAP_FACE",FACE,{"disambiguationData":[OSD([subQ1,sQuery(id+"F12.wireOp",EDGE,"E10.1.0")])],"isStart":false}),makeQuery(id+"F13.opExtrude","CAP_FACE",FACE,{"disambiguationData":[OSD([subQ1,sQuery(id+"F12.wireOp",EDGE,"E10.2.0")])],"isStart":false}),makeQuery(id+"F13.opExtrude","CAP_FACE",FACE,{"disambiguationData":[OSD([subQ1,sQuery(id+"F12.wireOp",EDGE,"E10.3.0")])],"isStart":false}),makeQuery(id+"F13.opExtrude","CAP_FACE",FACE,{"disambiguationData":[OSD([subQ1,sQuery(id+"F12.wireOp",EDGE,"E10.4.0")])],"isStart":false}),makeQuery(id+"F13.opExtrude","CAP_FACE",FACE,{"disambiguationData":[OSD([subQ1,sQuery(id+"F12.wireOp",EDGE,"E10.5.0")])],"isStart":false}),makeQuery(id+"F13.opExtrude","CAP_FACE",FACE,{"disambiguationData":[OSD([subQ1,sQuery(id+"F12.wireOp",EDGE,"E10.6.0")])],"isStart":false}),makeQuery(id+"F13.opExtrude","SWEPT_FACE",FACE,{"disambiguationData":[OSD([subQ0])]}),makeQuery(id+"F13.opExtrude","CAP_FACE",FACE,{"disambiguationData":[OSD([subQ1,subQ0])],"isStart":false}),makeQuery(id+"F13.opExtrude","SWEPT_FACE",FACE,{"disambiguationData":[OSD([subQ2])]}),makeQuery(id+"F13.opExtrude","CAP_FACE",FACE,{"disambiguationData":[OSD([subQ1,subQ2])],"isStart":false}),makeQuery(id+"F13.opExtrude","CAP_FACE",FACE,{"disambiguationData":[OSD([subQ1,sQuery(id+"F12.wireOp",EDGE,"E10.9.0")])],"isStart":false})])],"derivedFrom":makeQuery(id+"F7.opExtrude","CAP_EDGE",EDGE,{"disambiguationData":[OSD([subQ1])],"isStart":true})});}
            var Q17;
            Q17=makeQuery(id+"F13.opExtrude","CAP_EDGE",EDGE,{"disambiguationData":[OSD([sQuery(id+"F12.wireOp",EDGE,"E10.7.0")])],"isStart":false});
            var Q18;
            {var subQ0=sQuery(id+"F12.wireOp",EDGE,"E10.6.0");var subQ1=sQuery(id+"F6.wireOp",EDGE,"E4");var subQ2=sQuery(id+"F12.wireOp",EDGE,"E10.7.0");Q18=makeQuery(id+"F13.boolean.opBoolean","SPLIT",EDGE,{"disambiguationData":[TD([makeQuery(id+"F7.opExtrude","SWEPT_FACE",FACE,{"disambiguationData":[OSD([subQ1])]}),makeQuery(id+"F7.opExtrude","CAP_FACE",FACE,{"disambiguationData":[OSD([subQ1,sQuery(id+"F6.wireOp",EDGE,"E5")])],"isStart":true}),makeQuery(id+"F13.opExtrude","CAP_FACE",FACE,{"disambiguationData":[OSD([subQ1,sQuery(id+"F12.wireOp",EDGE,"E9")])],"isStart":false}),makeQuery(id+"F13.opExtrude","CAP_FACE",FACE,{"disambiguationData":[OSD([subQ1,sQuery(id+"F12.wireOp",EDGE,"E10.1.0")])],"isStart":false}),makeQuery(id+"F13.opExtrude","CAP_FACE",FACE,{"disambiguationData":[OSD([subQ1,sQuery(id+"F12.wireOp",EDGE,"E10.2.0")])],"isStart":false}),makeQuery(id+"F13.opExtrude","CAP_FACE",FACE,{"disambiguationData":[OSD([subQ1,sQuery(id+"F12.wireOp",EDGE,"E10.3.0")])],"isStart":false}),makeQuery(id+"F13.opExtrude","CAP_FACE",FACE,{"disambiguationData":[OSD([subQ1,sQuery(id+"F12.wireOp",EDGE,"E10.4.0")])],"isStart":false}),makeQuery(id+"F13.opExtrude","CAP_FACE",FACE,{"disambiguationData":[OSD([subQ1,sQuery(id+"F12.wireOp",EDGE,"E10.5.0")])],"isStart":false}),makeQuery(id+"F13.opExtrude","SWEPT_FACE",FACE,{"disambiguationData":[OSD([subQ0])]}),makeQuery(id+"F13.opExtrude","CAP_FACE",FACE,{"disambiguationData":[OSD([subQ1,subQ0])],"isStart":false}),makeQuery(id+"F13.opExtrude","SWEPT_FACE",FACE,{"disambiguationData":[OSD([subQ2])]}),makeQuery(id+"F13.opExtrude","CAP_FACE",FACE,{"disambiguationData":[OSD([subQ1,subQ2])],"isStart":false}),makeQuery(id+"F13.opExtrude","CAP_FACE",FACE,{"disambiguationData":[OSD([subQ1,sQuery(id+"F12.wireOp",EDGE,"E10.8.0")])],"isStart":false}),makeQuery(id+"F13.opExtrude","CAP_FACE",FACE,{"disambiguationData":[OSD([subQ1,sQuery(id+"F12.wireOp",EDGE,"E10.9.0")])],"isStart":false})])],"derivedFrom":makeQuery(id+"F7.opExtrude","CAP_EDGE",EDGE,{"disambiguationData":[OSD([subQ1])],"isStart":true})});}
            var Q19;
            Q19=makeQuery(id+"F13.opExtrude","CAP_EDGE",EDGE,{"disambiguationData":[OSD([sQuery(id+"F12.wireOp",EDGE,"E10.6.0")])],"isStart":false});
            chamfer(context, id + "F15", {"entities" : qUnion([Q0, Q1, Q2, Q3, Q4, Q5, Q6, Q7, Q8, Q9, Q10, Q11, Q12, Q13, Q14, Q15, Q16, Q17, Q18, Q19]), "width" : 0.7 * mm, "tangentPropagation" : true});
        }
        {
            var Q0;
            Q0=makeQuery(id+"F5.opExtrude","CAP_EDGE",EDGE,{"disambiguationData":[OSD([sQuery(id+"F4.wireOp",EDGE,"E3")])],"isStart":true});
            chamfer(context, id + "F16", {"entities" : qUnion([Q0]), "width" : 6.75 * mm, "tangentPropagation" : true});
        }
        {
            var Q0;
            Q0=makeQuery(id+"F9.opExtrude","CAP_EDGE",EDGE,{"disambiguationData":[OSD([sQuery(id+"F0.wireOp",EDGE,"E1")])],"isStart":false});
            var Q1;
            Q1=makeQuery(id+"F9.opExtrude","CAP_EDGE",EDGE,{"disambiguationData":[OSD([sQuery(id+"F8.wireOp",EDGE,"E6")])],"isStart":false});
            chamfer(context, id + "F17", {"entities" : qUnion([Q0, Q1]), "width" : 1.3 * mm, "tangentPropagation" : true});
        }
    });
